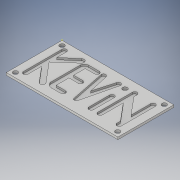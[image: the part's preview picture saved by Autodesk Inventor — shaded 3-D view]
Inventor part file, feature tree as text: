
AUTODESK INVENTOR PART (.ipt)
format: ipt  version: 2017 (Build 210142000, 142)  size: 186,880 bytes
history: native  units: in
note: dims shown in document units (in); Inventor stores cm internally (conversion verified against a paired STEP export)
features: sketch x6, extrude x2, hole x1
ambient origin geometry x8: Origin, YZ Plane, XZ Plane, XY Plane, X Axis, Y Axis, Z Axis, Center Point
bodies: Solid1 (feature_tree)
feature tree (9):
  extrude  "Extrusion1"  Depth=0.1in TaperAngle=0.0deg
  sketch  "Sketch2"  dims[d10=0.25in d11=0.75in d12=0.119in d13=0.25in d14=0.5635in d15=1.0in d16=0.8108in d59=0.1in d60=0.0in]
  sketch  "Sketch3"
  hole  "Hole1"  [1 undecoded]
  sketch  "Sketch5"
  sketch  "Sketch6"
  extrude  "Extrusion2"  [1 undecoded]
  sketch  "Sketch1"  dims[d2=0.125in d3=0.0in]
  sketch  "Sketch4"
note: 2 required parameter values undecoded (feature->parameter linkage not recoverable at this tier; creation-order binding heuristic only, values carry confidence <= 0.55)
